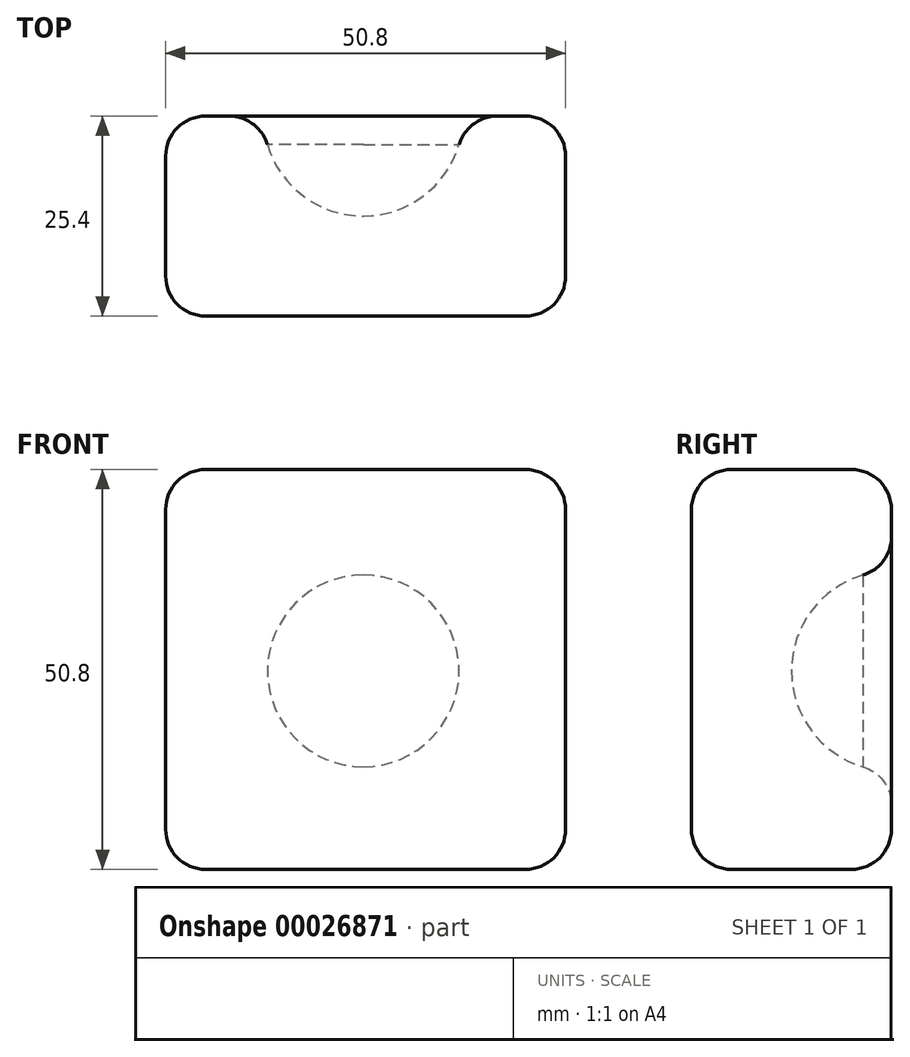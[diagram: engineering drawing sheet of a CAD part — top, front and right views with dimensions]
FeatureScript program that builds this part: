
annotation { "Feature Type Name" : "Feature", "Feature Type Description" : "" }
export const myFeature = defineFeature(function(context is Context, id is Id, definition is map)
    precondition{}
    {
        {
            var Q0;
            Q0=qCreatedBy(makeId("Front.planeOp"),FACE);
            var sketch = newSketch(context, id + "F0", { "sketchPlane" : qUnion([Q0])});
            skLineSegment(sketch, "E0.bottom", {"start": v(-58.84, -6.22) * mm, "end": v(-8.04, -6.22) * mm});
            skLineSegment(sketch, "E0.top", {"start": v(-58.84, -57.02) * mm, "end": v(-8.04, -57.02) * mm});
            skLineSegment(sketch, "E0.left", {"start": v(-58.84, -6.22) * mm, "end": v(-58.84, -57.02) * mm});
            skLineSegment(sketch, "E0.right", {"start": v(-8.04, -6.22) * mm, "end": v(-8.04, -57.02) * mm});
            skPoint(sketch, "E1.start.orphan", {"position": v(-33.54, -18.55) * mm});
            skPoint(sketch, "E2.center.orphan", {"position": v(-33.54, -31.25) * mm});
            skSolve(sketch);
        }
        {
            var Q0;
            Q0=makeQuery(id+"F0.imprint","IMPRINT",FACE,{"disambiguationData":[TD([[makeQuery(id+"F0.imprint","IMPRINT",EDGE,{"derivedFrom":sQuery(id+"F0.wireOp",EDGE,"E0.bottom")}),-1.0]])]});
            extrude(context, id + "F1", {"entities" : qUnion([Q0]), "depth" : 25.4 * mm});
        }
        {
            var Q0;
            Q0=qCreatedBy(makeId("Front.planeOp"),FACE);
            var sketch = newSketch(context, id + "F2", { "sketchPlane" : qUnion([Q0])});
            skCircle(sketch, "E3", {"center": v(-33.73, -31.8) * mm, "radius": 12.7 * mm});
            skLineSegment(sketch, "E4", {"start": v(-33.73, -19.1) * mm, "end": v(-33.73, -44.5) * mm});
            skSolve(sketch);
        }
        {
            var Q0;
            {var subQ0=sQuery(id+"F2.wireOp",EDGE,"E4");Q0=makeQuery(id+"F2.imprint","IMPRINT",FACE,{"disambiguationData":[TD([[makeQuery(id+"F2.imprint","IMPRINT",EDGE,{"derivedFrom":subQ0}),-1.0]])]});}
            var Q1;
            Q1=sQuery(id+"F2.wireOp",EDGE,"E4");
            revolve(context, id + "F3", {"operationType" : NewBodyOperationType.REMOVE, "entities" : qUnion([Q0]), "axis" : qUnion([Q1]), "revolveType" : RevolveType.FULL, "oppositeDirection" : true});
        }
        {
            var Q0;
            Q0=makeQuery(id+"F1.opExtrude","CAP_FACE",FACE,{"disambiguationData":[OSD([sQuery(id+"F0.wireOp",EDGE,"E0.bottom"),sQuery(id+"F0.wireOp",EDGE,"E0.top"),sQuery(id+"F0.wireOp",EDGE,"E0.left"),sQuery(id+"F0.wireOp",EDGE,"E0.right")])],"isStart":false});
            var Q1;
            Q1=makeQuery(id+"F1.opExtrude","SWEPT_FACE",FACE,{"disambiguationData":[OSD([sQuery(id+"F0.wireOp",EDGE,"E0.right")])]});
            var Q2;
            Q2=makeQuery(id+"F1.opExtrude","SWEPT_FACE",FACE,{"disambiguationData":[OSD([sQuery(id+"F0.wireOp",EDGE,"E0.bottom")])]});
            var Q3;
            Q3=makeQuery(id+"F1.opExtrude","SWEPT_EDGE",EDGE,{"disambiguationData":[OSD([sQuery(id+"F0.wireOp",EDGE,"E0.top"),sQuery(id+"F0.wireOp",EDGE,"E0.left")])]});
            var Q4;
            Q4=makeQuery(id+"F1.opExtrude","SWEPT_EDGE",EDGE,{"disambiguationData":[OSD([sQuery(id+"F0.wireOp",EDGE,"E0.top"),sQuery(id+"F0.wireOp",EDGE,"E0.right")])]});
            var Q5;
            Q5=makeQuery(id+"F1.opExtrude","CAP_EDGE",EDGE,{"disambiguationData":[OSD([sQuery(id+"F0.wireOp",EDGE,"E0.top")])],"isStart":true});
            var Q6;
            Q6=makeQuery(id+"F1.opExtrude","CAP_EDGE",EDGE,{"disambiguationData":[OSD([sQuery(id+"F0.wireOp",EDGE,"E0.top")])],"isStart":false});
            var Q7;
            Q7=makeQuery(id+"F1.opExtrude","CAP_FACE",FACE,{"disambiguationData":[OSD([sQuery(id+"F0.wireOp",EDGE,"E0.bottom"),sQuery(id+"F0.wireOp",EDGE,"E0.top"),sQuery(id+"F0.wireOp",EDGE,"E0.left"),sQuery(id+"F0.wireOp",EDGE,"E0.right")])],"isStart":true});
            fillet(context, id + "F4", {"entities" : qUnion([Q0, Q1, Q2, Q3, Q4, Q5, Q6, Q7]), "radius" : 5.08 * mm, "tangentPropagation" : true, "allowEdgeOverflow" : false});
        }
    });
